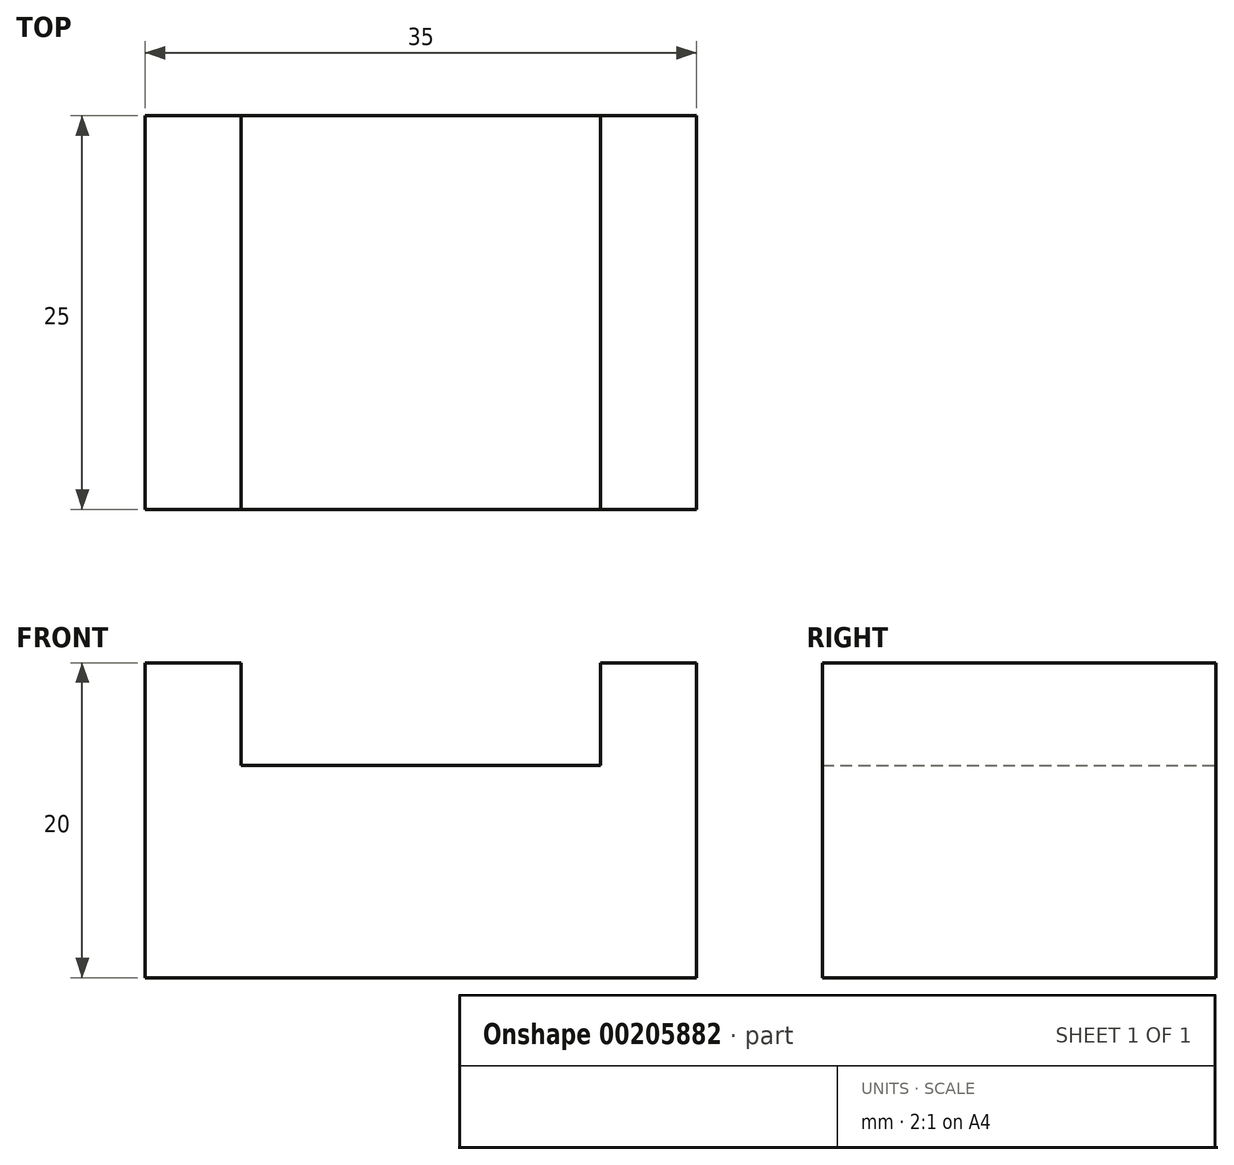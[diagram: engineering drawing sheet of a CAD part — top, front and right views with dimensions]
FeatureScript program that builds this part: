
annotation { "Feature Type Name" : "Feature", "Feature Type Description" : "" }
export const myFeature = defineFeature(function(context is Context, id is Id, definition is map)
    precondition{}
    {
        {
            var Q0;
            Q0=qCreatedBy(makeId("Front.planeOp"),FACE);
            var sketch = newSketch(context, id + "F0", { "sketchPlane" : qUnion([Q0])});
            skLineSegment(sketch, "E0.bottom", {"start": v(11.4, 6.75) * mm, "end": v(-11.4, 6.75) * mm});
            skLineSegment(sketch, "E0.top", {"start": v(17.5, -6.75) * mm, "end": v(-17.5, -6.75) * mm});
            skLineSegment(sketch, "E0.left", {"start": v(17.5, 6.75) * mm, "end": v(17.5, -6.75) * mm});
            skLineSegment(sketch, "E0.right", {"start": v(-17.5, 6.75) * mm, "end": v(-17.5, -6.75) * mm});
            skPoint(sketch, "E0.middle", {"position": v(0, 0) * mm});
            skLineSegment(sketch, "E1.top", {"start": v(-17.5, 13.25) * mm, "end": v(-11.4, 13.25) * mm});
            skLineSegment(sketch, "E1.right", {"start": v(-11.4, 6.75) * mm, "end": v(-11.4, 13.25) * mm});
            skLineSegment(sketch, "E2", {"start": v(-17.5, 13.25) * mm, "end": v(-17.5, 6.75) * mm});
            skLineSegment(sketch, "E3.MirrorCS", {"start": v(17.5, 13.25) * mm, "end": v(11.4, 13.25) * mm});
            skLineSegment(sketch, "E4.MirrorCS", {"start": v(17.5, 13.25) * mm, "end": v(17.5, 6.75) * mm});
            skLineSegment(sketch, "E5.MirrorCS", {"start": v(11.4, 6.75) * mm, "end": v(11.4, 13.25) * mm});
            skPoint(sketch, "E6.orphan", {"position": v(0, 6.75) * mm});
            skPoint(sketch, "E7.end.orphan", {"position": v(0, -6.75) * mm});
            skSolve(sketch);
        }
        {
            var Q0;
            Q0=makeQuery(id+"F0.imprint","IMPRINT",FACE,{"disambiguationData":[TD([[makeQuery(id+"F0.imprint","IMPRINT",EDGE,{"derivedFrom":sQuery(id+"F0.wireOp",EDGE,"E0.bottom")}),1.0]])]});
            extrude(context, id + "F1", {"entities" : qUnion([Q0]), "depth" : 25 * mm});
        }
    });
